# Revit family: EHW214C
name_source: partatom
category: Plumbing Fixtures
units: mm (PartAtom-declared; Revit-internal decimal feet)

## family parameters
Always vertical = Yes
Cut with Voids When Loaded = No
OmniClass Number = 23.45.00.00
OmniClass Title = Sanitary, Laundry, and Cleaning Equipment
Part Type = Normal
Room Calculation Point = No
Round Connector Dimension = Use Diameter
Shared = No
Work Plane-Based = No

## types (2) — shared parameters
Activation by = Mechanical Front Bubbler Button
Assembly Code = D2010810
BUBBLER_MATERIAL = Metal - Steel - Stainless - Chrome
BUTTON_MATERIAL = Metal - Steel - Stainless - Chrome
CW Connection = Yes
Chilling Option = Non-refrigerated
DRAIN_MATERIAL = Metal - Steel - Stainless - Chrome
Description = Elkay Soft Sides Bi-Level Composite Fountain Non-Filtered, Non-Refrigerated White Granite Composite
Drain_Pipe 1 1/2" = 38 mm
HW Connection = No
Inlet_Pipe = 10 mm  [stored 0.0328084 ft]
Installation Location = Indoor + Outdoor
Manufacturer = Elkay
Mounting Type = Wall Mount (On Wall)
No. of Stations Served = 1
SINK_MATERIAL = Metal - Steel - Stainless - Chrome
Special Feature = -
Vent Connection = No
Version = 1.0.0.0
Waste Connection = Yes

## per-type parameters (varying)
| type | Approx. Shipping Weight | BODY_MATERIAL | Bubbler Style | Finish | Model |
| HRFG-EBP (GRY) | 59 lbs. | Gray Marblyte (GRY) | Double Bubbler | Gray Marblyte (GRY) | 7433004661 |
| EHW214FPK | 46 lbs. | Metal - Steel - Stainless - Chrome | Vandal Resistant | Stainless Steel | EHW214FPK |

note: [stored X ft] marks values corroborated as IEEE doubles in the binary element streams (Revit-internal decimal feet)

## geometry (parser evidence)
native form markers: Sweep x23
no freeform markers — native parametric forms only
